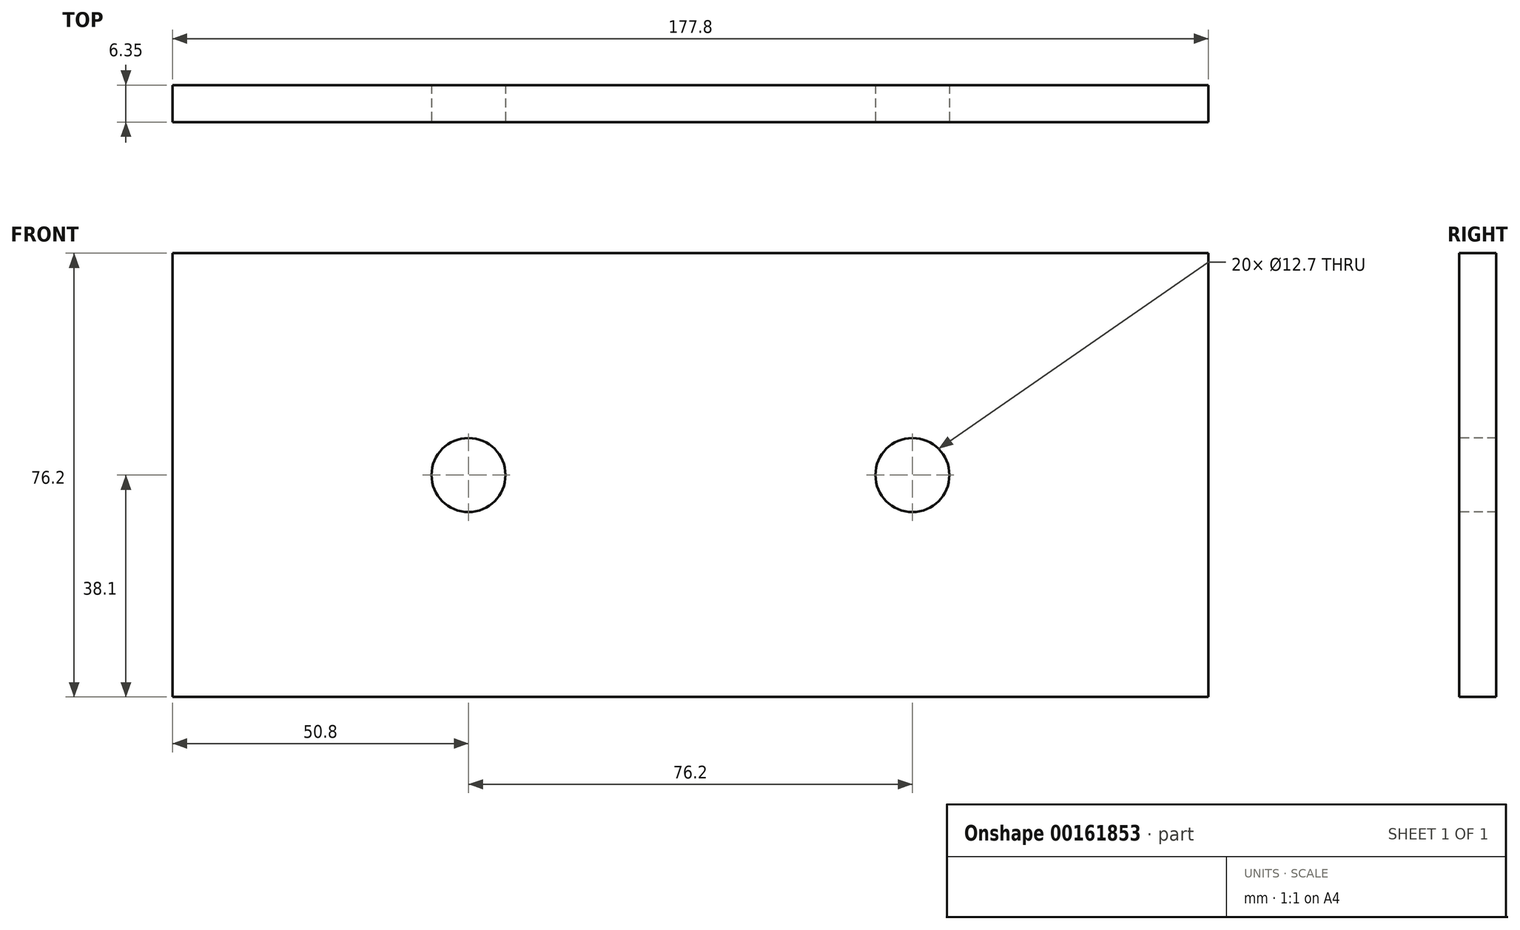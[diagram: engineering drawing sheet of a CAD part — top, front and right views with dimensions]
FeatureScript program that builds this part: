
annotation { "Feature Type Name" : "Feature", "Feature Type Description" : "" }
export const myFeature = defineFeature(function(context is Context, id is Id, definition is map)
    precondition{}
    {
        {
            var Q0;
            Q0=qCreatedBy(makeId("Front.planeOp"),FACE);
            var sketch = newSketch(context, id + "F0", { "sketchPlane" : qUnion([Q0])});
            skLineSegment(sketch, "E0.bottom", {"start": v(0, 0) * mm, "end": v(177.8, 0) * mm});
            skLineSegment(sketch, "E0.top", {"start": v(0, -76.2) * mm, "end": v(177.8, -76.2) * mm});
            skLineSegment(sketch, "E0.left", {"start": v(0, 0) * mm, "end": v(0, -76.2) * mm});
            skLineSegment(sketch, "E0.right", {"start": v(177.8, 0) * mm, "end": v(177.8, -76.2) * mm});
            skSolve(sketch);
        }
        {
            var Q0;
            Q0=qSketchRegion(id+"F0",true);
            extrude(context, id + "F1", {"entities" : qUnion([Q0]), "depth" : 6.35 * mm});
        }
        {
            var Q0;
            Q0=makeQuery(id+"F1.opExtrude","CAP_FACE",FACE,{"disambiguationData":[OSD([sQuery(id+"F0.wireOp",EDGE,"E0.bottom"),sQuery(id+"F0.wireOp",EDGE,"E0.top"),sQuery(id+"F0.wireOp",EDGE,"E0.left"),sQuery(id+"F0.wireOp",EDGE,"E0.right")])],"isStart":false});
            var sketch = newSketch(context, id + "F2", { "sketchPlane" : qUnion([Q0])});
            skLineSegment(sketch, "E1", {"start": v(0, -38.1) * mm, "end": v(177.8, -38.1) * mm});
            skLineSegment(sketch, "E2", {"start": v(50.8, 0) * mm, "end": v(50.8, -76.2) * mm});
            skLineSegment(sketch, "E3", {"start": v(127, 0) * mm, "end": v(127, -76.2) * mm});
            skCircle(sketch, "E4", {"center": v(50.8, -38.1) * mm, "radius": 6.35 * mm});
            skCircle(sketch, "E5", {"center": v(127, -38.1) * mm, "radius": 6.35 * mm});
            skSolve(sketch);
        }
        {
            var Q0;
            Q0=qSketchRegion(id+"F2",true);
            extrude(context, id + "F3", {"entities" : qUnion([Q0]), "operationType" : NewBodyOperationType.REMOVE, "endBound" : BoundingType.THROUGH_ALL, "oppositeDirection" : true, "depth" : 9.52 * mm});
        }
    });
